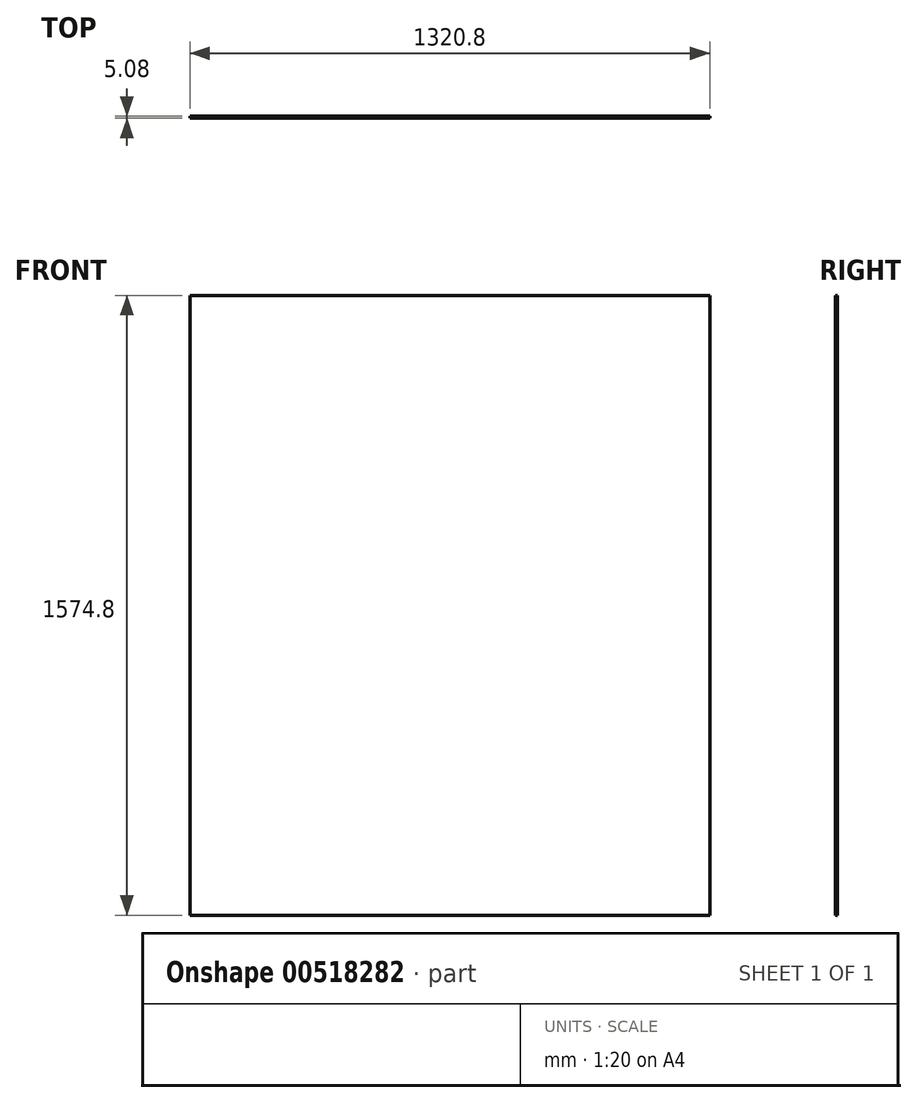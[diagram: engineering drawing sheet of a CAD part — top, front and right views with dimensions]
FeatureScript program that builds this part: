
annotation { "Feature Type Name" : "Feature", "Feature Type Description" : "" }
export const myFeature = defineFeature(function(context is Context, id is Id, definition is map)
    precondition{}
    {
        {
            var Q0;
            Q0=qCreatedBy(makeId("Front.planeOp"),FACE);
            var sketch = newSketch(context, id + "F0", { "sketchPlane" : qUnion([Q0])});
            skLineSegment(sketch, "E0.bottom", {"start": v(-681.83, 809.34) * mm, "end": v(638.97, 809.34) * mm});
            skLineSegment(sketch, "E0.top", {"start": v(-681.83, -765.46) * mm, "end": v(638.97, -765.46) * mm});
            skLineSegment(sketch, "E0.left", {"start": v(-681.83, 809.34) * mm, "end": v(-681.83, -765.46) * mm});
            skLineSegment(sketch, "E0.right", {"start": v(638.97, 809.34) * mm, "end": v(638.97, -765.46) * mm});
            skSolve(sketch);
        }
        {
            var Q0;
            Q0=makeQuery(id+"F0.imprint","IMPRINT",FACE,{"disambiguationData":[TD([[makeQuery(id+"F0.imprint","IMPRINT",EDGE,{"derivedFrom":sQuery(id+"F0.wireOp",EDGE,"E0.bottom")}),-1.0]])]});
            extrude(context, id + "F1", {"entities" : qUnion([Q0]), "depth" : 5.08 * mm, "offsetDistance" : 25.4 * mm});
        }
    });
